# Revit family: WBY_A3-4-UNIT-BOW
name_source: partatom
category: Windows
revit_build: Autodesk Revit 2016 (Build: 20150220_1215(x64)
units: mm (PartAtom-declared; Revit-internal decimal feet)

## family parameters
Always vertical = Yes
Cut with Voids When Loaded = No
Host = Wall
Room Calculation Point = No
Shared = No

## types (6) — shared parameters
Height = 4' - 0"
JAMB THICKNESS = 0' - 0 3/4"
T.O. HEAD = 7' - 0"
Wall Closure = By host

## per-type parameters (varying)
| type | CENTER ADJUST | JAMB DEPTH | PROJECTION | RADIUS | SIDE ADJUST | Width |
| 17" FRAME, EA | 0' - 0 27/32" | 0' - 5" | 0' - 7 7/8" | 6' - 4" | 1' - 4 7/16" | 5' - 9 1/8" |
| 21" FRAME, EA | 0' - 0 25/32" | 0' - 4 1/2" | 0' - 9 5/8" | 7' - 10" | 1' - 8 3/8" | 7' - 0 5/8" |
| 23" FRAME, EA | 0' - 0 27/32" | 0' - 4 1/2" | 0' - 10 3/8" | 8' - 7" | 1' - 10 1/4" | 7' - 8 3/8" |
| 25" FRAME, EA | 0' - 0 29/32" | 0' - 4 1/2" | 0' - 11 3/8" | 9' - 4" | 2' - 0 1/8" | 8' - 4 1/8" |
| 29" FRAME, EA. | 0' - 0 31/32" | 0' - 4 1/2" | 1' - 1 1/8" | 10' - 9 3/4" | 2' - 3 15/16" | 9' - 7 5/8" |
| 35" FRAME, EA | 0' - 1 5/32" | 0' - 4 1/2" | 1' - 3 3/4" | 13' - 0 5/8" | 2' - 9 9/16" | 11' - 6 7/8" |

## geometry (parser evidence)
native form markers: Sweep x2
no freeform markers — native parametric forms only
